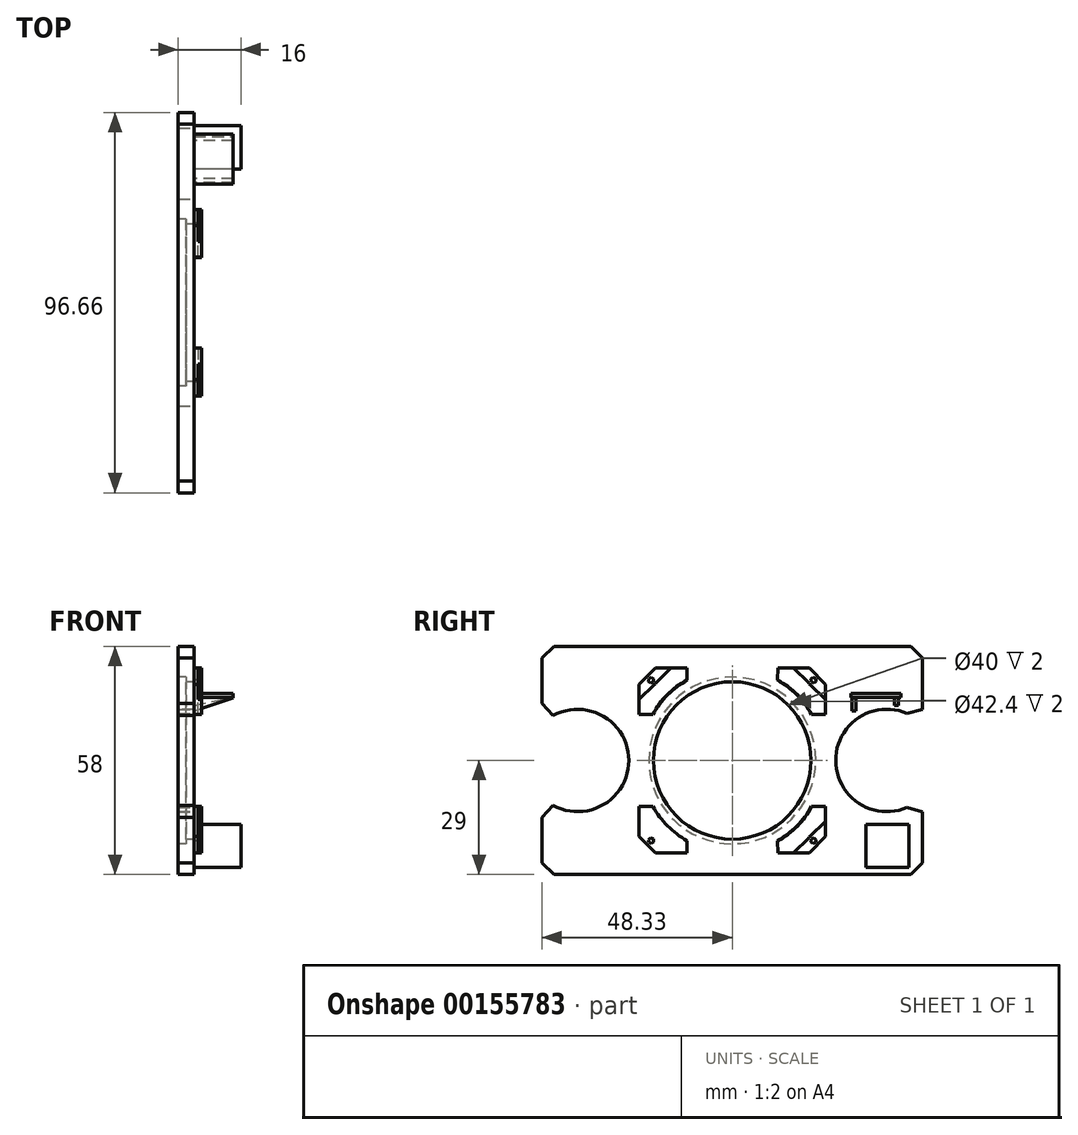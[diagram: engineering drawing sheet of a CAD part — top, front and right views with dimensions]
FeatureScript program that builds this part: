
annotation { "Feature Type Name" : "Feature", "Feature Type Description" : "" }
export const myFeature = defineFeature(function(context is Context, id is Id, definition is map)
    precondition{}
    {
        {
            var Q0;
            Q0=qCreatedBy(makeId("Right.planeOp"),FACE);
            var sketch = newSketch(context, id + "F0", { "sketchPlane" : qUnion([Q0])});
            skLineSegment(sketch, "E0", {"start": v(-0.17, 29) * mm, "end": v(48.33, 29) * mm});
            skCircle(sketch, "E1", {"center": v(0, 0) * mm, "radius": 20 * mm});
            skLineSegment(sketch, "E2", {"start": v(-71.24, 0) * mm, "end": v(71.03, 0) * mm, "construction": true});
            skLineSegment(sketch, "E3", {"start": v(0, -43.54) * mm, "end": v(0, 44.78) * mm, "construction": true});
            skLineSegment(sketch, "E4", {"start": v(48.33, 29) * mm, "end": v(48.33, 0) * mm});
            skLineSegment(sketch, "E5.MirrorCS", {"start": v(0.17, 29) * mm, "end": v(-48.33, 29) * mm});
            skLineSegment(sketch, "E6.MirrorCS", {"start": v(-48.33, 29) * mm, "end": v(-48.33, 0) * mm});
            skLineSegment(sketch, "E7.MirrorCS", {"start": v(-48.33, -29) * mm, "end": v(-48.33, 0) * mm});
            skLineSegment(sketch, "E8.MirrorCS", {"start": v(0.17, -29) * mm, "end": v(-48.33, -29) * mm});
            skLineSegment(sketch, "E9.MirrorCS", {"start": v(-0.17, -29) * mm, "end": v(48.33, -29) * mm});
            skLineSegment(sketch, "E10.MirrorCS", {"start": v(48.33, -29) * mm, "end": v(48.33, 0) * mm});
            skLineSegment(sketch, "E11", {"start": v(-65.88, 28) * mm, "end": v(62.3, 28) * mm, "construction": true});
            skLineSegment(sketch, "E12.MirrorCS", {"start": v(-65.88, -28) * mm, "end": v(62.3, -28) * mm, "construction": true});
            skSolve(sketch);
        }
        {
            var Q0;
            Q0 = qSketchRegion(id + "F0", true);
            extrude(context, id + "F1", {"entities" : qUnion([Q0]), "depth" : 4 * mm});
        }
        {
            var Q0;
            Q0=makeQuery(id+"F1.opExtrude","CAP_FACE",FACE,{"disambiguationData":[OSD([sQuery(id+"F0.wireOp",EDGE,"E0"),sQuery(id+"F0.wireOp",EDGE,"E1"),sQuery(id+"F0.wireOp",EDGE,"E4"),sQuery(id+"F0.wireOp",EDGE,"E5.MirrorCS"),sQuery(id+"F0.wireOp",EDGE,"E6.MirrorCS"),sQuery(id+"F0.wireOp",EDGE,"E7.MirrorCS"),sQuery(id+"F0.wireOp",EDGE,"E8.MirrorCS"),sQuery(id+"F0.wireOp",EDGE,"E9.MirrorCS"),sQuery(id+"F0.wireOp",EDGE,"E10.MirrorCS")])],"isStart":false});
            var sketch = newSketch(context, id + "F2", { "sketchPlane" : qUnion([Q0])});
            skCircle(sketch, "E13", {"center": v(-39.28, 0) * mm, "radius": 13 * mm});
            skLineSegment(sketch, "E14", {"start": v(0, 41.82) * mm, "end": v(0, -40.06) * mm, "construction": true});
            skLineSegment(sketch, "E15", {"start": v(59.88, 0) * mm, "end": v(-62, 0) * mm, "construction": true});
            skCircle(sketch, "E16.MirrorC", {"center": v(39.28, 0) * mm, "radius": 13 * mm});
            skSolve(sketch);
        }
        {
            var Q0;
            Q0 = qSketchRegion(id + "F2", true);
            extrude(context, id + "F3", {"entities" : qUnion([Q0]), "operationType" : NewBodyOperationType.REMOVE, "oppositeDirection" : true, "depth" : 5 * mm});
        }
        {
            var Q0;
            Q0=makeQuery(id+"F3.boolean.opBoolean","INTERSECT",EDGE,{"disambiguationData":[OD(1.0)],"derivedFrom":[makeQuery(id+"F1.opExtrude","SWEPT_FACE",FACE,{"disambiguationData":[OSD([sQuery(id+"F0.wireOp",EDGE,"E4"),sQuery(id+"F0.wireOp",EDGE,"E10.MirrorCS")])]}),makeQuery(id+"F3.opExtrude","SWEPT_FACE",FACE,{"disambiguationData":[OSD([sQuery(id+"F2.wireOp",EDGE,"E16.MirrorC")])]})]});
            var Q1;
            Q1=makeQuery(id+"F3.boolean.opBoolean","INTERSECT",EDGE,{"disambiguationData":[OD(0.0)],"derivedFrom":[makeQuery(id+"F1.opExtrude","SWEPT_FACE",FACE,{"disambiguationData":[OSD([sQuery(id+"F0.wireOp",EDGE,"E4"),sQuery(id+"F0.wireOp",EDGE,"E10.MirrorCS")])]}),makeQuery(id+"F3.opExtrude","SWEPT_FACE",FACE,{"disambiguationData":[OSD([sQuery(id+"F2.wireOp",EDGE,"E16.MirrorC")])]})]});
            chamfer(context, id + "F4", {"entities" : qUnion([Q0, Q1]), "chamferType" : ChamferType.TWO_OFFSETS, "width1" : 6 * mm, "oppositeDirection" : true, "width2" : 5 * mm, "tangentPropagation" : true});
        }
        {
            var Q0;
            Q0=makeQuery(id+"F3.boolean.opBoolean","INTERSECT",EDGE,{"disambiguationData":[OD(1.0)],"derivedFrom":[makeQuery(id+"F1.opExtrude","SWEPT_FACE",FACE,{"disambiguationData":[OSD([sQuery(id+"F0.wireOp",EDGE,"E6.MirrorCS"),sQuery(id+"F0.wireOp",EDGE,"E7.MirrorCS")])]}),makeQuery(id+"F3.opExtrude","SWEPT_FACE",FACE,{"disambiguationData":[OSD([sQuery(id+"F2.wireOp",EDGE,"E13")])]})]});
            var Q1;
            Q1=makeQuery(id+"F3.boolean.opBoolean","INTERSECT",EDGE,{"disambiguationData":[OD(0.0)],"derivedFrom":[makeQuery(id+"F1.opExtrude","SWEPT_FACE",FACE,{"disambiguationData":[OSD([sQuery(id+"F0.wireOp",EDGE,"E6.MirrorCS"),sQuery(id+"F0.wireOp",EDGE,"E7.MirrorCS")])]}),makeQuery(id+"F3.opExtrude","SWEPT_FACE",FACE,{"disambiguationData":[OSD([sQuery(id+"F2.wireOp",EDGE,"E13")])]})]});
            chamfer(context, id + "F5", {"entities" : qUnion([Q0, Q1]), "chamferType" : ChamferType.TWO_OFFSETS, "width1" : 5 * mm, "oppositeDirection" : true, "width2" : 6 * mm, "tangentPropagation" : true});
        }
        {
            var Q0;
            Q0=makeQuery(id+"F1.opExtrude","SWEPT_EDGE",EDGE,{"disambiguationData":[OSD([sQuery(id+"F0.wireOp",EDGE,"E5.MirrorCS"),sQuery(id+"F0.wireOp",EDGE,"E6.MirrorCS")])]});
            var Q1;
            Q1=makeQuery(id+"F1.opExtrude","SWEPT_EDGE",EDGE,{"disambiguationData":[OSD([sQuery(id+"F0.wireOp",EDGE,"E0"),sQuery(id+"F0.wireOp",EDGE,"E4")])]});
            var Q2;
            Q2=makeQuery(id+"F1.opExtrude","SWEPT_EDGE",EDGE,{"disambiguationData":[OSD([sQuery(id+"F0.wireOp",EDGE,"E9.MirrorCS"),sQuery(id+"F0.wireOp",EDGE,"E10.MirrorCS")])]});
            var Q3;
            Q3=makeQuery(id+"F1.opExtrude","SWEPT_EDGE",EDGE,{"disambiguationData":[OSD([sQuery(id+"F0.wireOp",EDGE,"E7.MirrorCS"),sQuery(id+"F0.wireOp",EDGE,"E8.MirrorCS")])]});
            chamfer(context, id + "F6", {"entities" : qUnion([Q0, Q1, Q2, Q3]), "width" : 3 * mm, "tangentPropagation" : true});
        }
        {
            var Q0;
            Q0=makeQuery(id+"F1.opExtrude","CAP_FACE",FACE,{"disambiguationData":[OSD([sQuery(id+"F0.wireOp",EDGE,"E0"),sQuery(id+"F0.wireOp",EDGE,"E1"),sQuery(id+"F0.wireOp",EDGE,"E4"),sQuery(id+"F0.wireOp",EDGE,"E5.MirrorCS"),sQuery(id+"F0.wireOp",EDGE,"E6.MirrorCS"),sQuery(id+"F0.wireOp",EDGE,"E7.MirrorCS"),sQuery(id+"F0.wireOp",EDGE,"E8.MirrorCS"),sQuery(id+"F0.wireOp",EDGE,"E9.MirrorCS"),sQuery(id+"F0.wireOp",EDGE,"E10.MirrorCS")])],"isStart":false});
            var sketch = newSketch(context, id + "F7", { "sketchPlane" : qUnion([Q0])});
            skSolve(sketch);
        }
        {
            var Q0;
            {var subQ7=sQuery(id+"F0.wireOp",EDGE,"E1");Q0=makeQuery(id+"F7.imprint","IMPRINT",FACE,{"disambiguationData":[TD([[makeQuery(id+"F7.imprint","IMPRINT",EDGE,{"derivedFrom":makeQuery(id+"F1.opExtrude","CAP_EDGE",EDGE,{"disambiguationData":[OSD([subQ7])],"isStart":false})}),-1.0]])]});}
            var sketch = newSketch(context, id + "F8", { "sketchPlane" : qUnion([Q0])});
            skLineSegment(sketch, "E17", {"start": v(0, 45.22) * mm, "end": v(0, -42.28) * mm, "construction": true});
            skLineSegment(sketch, "E18", {"start": v(53.44, 0) * mm, "end": v(-45.28, 0) * mm, "construction": true});
            skLineSegment(sketch, "E19", {"start": v(-23.7, 19.27) * mm, "end": v(-23.67, 11.67) * mm});
            skLineSegment(sketch, "E20", {"start": v(-23.67, 11.67) * mm, "end": v(-20.17, 11.7) * mm});
            skLineSegment(sketch, "E21", {"start": v(-19.55, 23.47) * mm, "end": v(-11.55, 23.47) * mm});
            skLineSegment(sketch, "E22", {"start": v(-11.55, 23.47) * mm, "end": v(-11.5, 20.4) * mm});
            skArc(sketch, "E23", {"start": v(-11.5, 20.4) * mm, "mid": v(-16.43, 16.64) * mm, "end": v(-20.17, 11.7) * mm});
            skLineSegment(sketch, "E24", {"start": v(-19.55, 23.47) * mm, "end": v(-23.7, 19.27) * mm});
            skLineSegment(sketch, "E25", {"start": v(0, 0) * mm, "end": v(-36.4, 36.4) * mm, "construction": true});
            skLineSegment(sketch, "E26.MirrorCS", {"start": v(19.55, 23.47) * mm, "end": v(11.55, 23.47) * mm});
            skLineSegment(sketch, "E27.MirrorCS", {"start": v(11.55, 23.47) * mm, "end": v(11.5, 20.4) * mm});
            skLineSegment(sketch, "E28.MirrorCS", {"start": v(19.55, 23.47) * mm, "end": v(23.7, 19.27) * mm});
            skArc(sketch, "E29.MirrorCS", {"start": v(11.5, 20.4) * mm, "mid": v(16.43, 16.64) * mm, "end": v(20.17, 11.7) * mm});
            skLineSegment(sketch, "E30.MirrorCS", {"start": v(23.67, 11.67) * mm, "end": v(20.17, 11.7) * mm});
            skLineSegment(sketch, "E31.MirrorCS", {"start": v(23.7, 19.27) * mm, "end": v(23.67, 11.67) * mm});
            skLineSegment(sketch, "E32.MirrorCS", {"start": v(-23.67, -11.67) * mm, "end": v(-20.17, -11.7) * mm});
            skArc(sketch, "E33.MirrorCS", {"start": v(-11.5, -20.4) * mm, "mid": v(-16.43, -16.64) * mm, "end": v(-20.17, -11.7) * mm});
            skLineSegment(sketch, "E34.MirrorCS", {"start": v(-11.55, -23.47) * mm, "end": v(-11.5, -20.4) * mm});
            skLineSegment(sketch, "E35.MirrorCS", {"start": v(-19.55, -23.47) * mm, "end": v(-11.55, -23.47) * mm});
            skLineSegment(sketch, "E36.MirrorCS", {"start": v(-19.55, -23.47) * mm, "end": v(-23.7, -19.27) * mm});
            skLineSegment(sketch, "E37.MirrorCS", {"start": v(-23.7, -19.27) * mm, "end": v(-23.67, -11.67) * mm});
            skLineSegment(sketch, "E38.MirrorCS", {"start": v(11.55, -23.47) * mm, "end": v(11.5, -20.4) * mm});
            skLineSegment(sketch, "E39.MirrorCS", {"start": v(19.55, -23.47) * mm, "end": v(11.55, -23.47) * mm});
            skLineSegment(sketch, "E40.MirrorCS", {"start": v(19.55, -23.47) * mm, "end": v(23.7, -19.27) * mm});
            skLineSegment(sketch, "E41.MirrorCS", {"start": v(23.7, -19.27) * mm, "end": v(23.67, -11.67) * mm});
            skLineSegment(sketch, "E42.MirrorCS", {"start": v(23.67, -11.67) * mm, "end": v(20.17, -11.7) * mm});
            skArc(sketch, "E43.MirrorCS", {"start": v(11.5, -20.4) * mm, "mid": v(16.43, -16.64) * mm, "end": v(20.17, -11.7) * mm});
            skSolve(sketch);
        }
        {
            var Q0;
            Q0 = qSketchRegion(id + "F8", true);
            extrude(context, id + "F9", {"entities" : qUnion([Q0]), "operationType" : NewBodyOperationType.ADD, "depth" : 1 * mm});
        }
        {
            var Q0;
            Q0=makeQuery(id+"F9.opExtrude","CAP_FACE",FACE,{"disambiguationData":[OSD([sQuery(id+"F8.wireOp",EDGE,"E19"),sQuery(id+"F8.wireOp",EDGE,"E20"),sQuery(id+"F8.wireOp",EDGE,"E21"),sQuery(id+"F8.wireOp",EDGE,"E22"),sQuery(id+"F8.wireOp",EDGE,"E23"),sQuery(id+"F8.wireOp",EDGE,"E24")])],"isStart":false});
            var sketch = newSketch(context, id + "F10", { "sketchPlane" : qUnion([Q0])});
            skLineSegment(sketch, "E44", {"start": v(0, 25.38) * mm, "end": v(0, -25.1) * mm, "construction": true});
            skLineSegment(sketch, "E45", {"start": v(28.15, 0) * mm, "end": v(-31.21, 0) * mm, "construction": true});
            skLineSegment(sketch, "E46", {"start": v(-15.55, 23.47) * mm, "end": v(-23.68, 15.47) * mm});
            skLineSegment(sketch, "E47", {"start": v(-23.68, 15.47) * mm, "end": v(-23.67, 11.67) * mm});
            skLineSegment(sketch, "E48", {"start": v(-23.67, 11.67) * mm, "end": v(-20.17, 11.7) * mm});
            skLineSegment(sketch, "E49", {"start": v(-15.55, 23.47) * mm, "end": v(-11.55, 23.47) * mm});
            skLineSegment(sketch, "E50", {"start": v(-11.55, 23.47) * mm, "end": v(-11.5, 20.4) * mm});
            skArc(sketch, "E51", {"start": v(-11.5, 20.4) * mm, "mid": v(-16.5, 16.71) * mm, "end": v(-20.17, 11.7) * mm});
            skLineSegment(sketch, "E52", {"start": v(-21.62, 21.37) * mm, "end": v(-16.43, 16.64) * mm, "construction": true});
            skCircle(sketch, "E53.cCircle", {"center": v(-20.17, 20.04) * mm, "radius": 0.8 * mm, "construction": true});
            skLineSegment(sketch, "E53.0", {"start": v(-21.04, 19.77) * mm, "end": v(-20.84, 20.66) * mm});
            skLineSegment(sketch, "E53.1", {"start": v(-20.84, 20.66) * mm, "end": v(-19.97, 20.94) * mm});
            skLineSegment(sketch, "E53.2", {"start": v(-19.97, 20.94) * mm, "end": v(-19.3, 20.32) * mm});
            skLineSegment(sketch, "E53.3", {"start": v(-19.3, 20.32) * mm, "end": v(-19.49, 19.43) * mm});
            skLineSegment(sketch, "E53.4", {"start": v(-19.49, 19.43) * mm, "end": v(-20.36, 19.15) * mm});
            skLineSegment(sketch, "E53.5", {"start": v(-20.36, 19.15) * mm, "end": v(-21.04, 19.77) * mm});
            skPoint(sketch, "E53.0.midPoint", {"position": v(-20.94, 20.21) * mm});
            skLineSegment(sketch, "E54.MirrorCS", {"start": v(11.55, 23.47) * mm, "end": v(11.5, 20.4) * mm});
            skLineSegment(sketch, "E55.MirrorCS", {"start": v(15.55, 23.47) * mm, "end": v(11.55, 23.47) * mm});
            skLineSegment(sketch, "E56.MirrorCS", {"start": v(15.55, 23.47) * mm, "end": v(23.68, 15.47) * mm});
            skLineSegment(sketch, "E57.MirrorCS", {"start": v(23.68, 15.47) * mm, "end": v(23.67, 11.67) * mm});
            skLineSegment(sketch, "E58.MirrorCS", {"start": v(23.67, 11.67) * mm, "end": v(20.17, 11.7) * mm});
            skArc(sketch, "E59.MirrorCS", {"start": v(11.5, 20.4) * mm, "mid": v(16.5, 16.71) * mm, "end": v(20.17, 11.7) * mm});
            skCircle(sketch, "E60.MirrorC", {"center": v(20.17, 20.04) * mm, "radius": 0.8 * mm, "construction": true});
            skLineSegment(sketch, "E61.MirrorCS", {"start": v(19.3, 20.32) * mm, "end": v(19.49, 19.43) * mm});
            skLineSegment(sketch, "E62.MirrorCS", {"start": v(19.49, 19.43) * mm, "end": v(20.36, 19.15) * mm});
            skLineSegment(sketch, "E63.MirrorCS", {"start": v(20.36, 19.15) * mm, "end": v(21.04, 19.77) * mm});
            skLineSegment(sketch, "E64.MirrorCS", {"start": v(21.04, 19.77) * mm, "end": v(20.84, 20.66) * mm});
            skLineSegment(sketch, "E65.MirrorCS", {"start": v(20.84, 20.66) * mm, "end": v(19.97, 20.94) * mm});
            skLineSegment(sketch, "E66.MirrorCS", {"start": v(19.97, 20.94) * mm, "end": v(19.3, 20.32) * mm});
            skLineSegment(sketch, "E67.MirrorCS", {"start": v(23.67, -11.67) * mm, "end": v(20.17, -11.7) * mm});
            skLineSegment(sketch, "E68.MirrorCS", {"start": v(23.68, -15.47) * mm, "end": v(23.67, -11.67) * mm});
            skLineSegment(sketch, "E69.MirrorCS", {"start": v(15.55, -23.47) * mm, "end": v(23.68, -15.47) * mm});
            skArc(sketch, "E70.MirrorCS", {"start": v(11.5, -20.4) * mm, "mid": v(16.5, -16.71) * mm, "end": v(20.17, -11.7) * mm});
            skLineSegment(sketch, "E71.MirrorCS", {"start": v(11.55, -23.47) * mm, "end": v(11.5, -20.4) * mm});
            skLineSegment(sketch, "E72.MirrorCS", {"start": v(15.55, -23.47) * mm, "end": v(11.55, -23.47) * mm});
            skLineSegment(sketch, "E73.MirrorCS", {"start": v(19.3, -20.32) * mm, "end": v(19.49, -19.43) * mm});
            skLineSegment(sketch, "E74.MirrorCS", {"start": v(19.97, -20.94) * mm, "end": v(19.3, -20.32) * mm});
            skLineSegment(sketch, "E75.MirrorCS", {"start": v(20.84, -20.66) * mm, "end": v(19.97, -20.94) * mm});
            skLineSegment(sketch, "E76.MirrorCS", {"start": v(21.04, -19.77) * mm, "end": v(20.84, -20.66) * mm});
            skLineSegment(sketch, "E77.MirrorCS", {"start": v(20.36, -19.15) * mm, "end": v(21.04, -19.77) * mm});
            skLineSegment(sketch, "E78.MirrorCS", {"start": v(19.49, -19.43) * mm, "end": v(20.36, -19.15) * mm});
            skArc(sketch, "E79.MirrorCS", {"start": v(-11.5, -20.4) * mm, "mid": v(-16.5, -16.71) * mm, "end": v(-20.17, -11.7) * mm});
            skLineSegment(sketch, "E80.MirrorCS", {"start": v(-11.55, -23.47) * mm, "end": v(-11.5, -20.4) * mm});
            skLineSegment(sketch, "E81.MirrorCS", {"start": v(-15.55, -23.47) * mm, "end": v(-11.55, -23.47) * mm});
            skLineSegment(sketch, "E82.MirrorCS", {"start": v(-15.55, -23.47) * mm, "end": v(-23.68, -15.47) * mm});
            skLineSegment(sketch, "E83.MirrorCS", {"start": v(-23.68, -15.47) * mm, "end": v(-23.67, -11.67) * mm});
            skLineSegment(sketch, "E84.MirrorCS", {"start": v(-23.67, -11.67) * mm, "end": v(-20.17, -11.7) * mm});
            skLineSegment(sketch, "E85.MirrorCS", {"start": v(-21.04, -19.77) * mm, "end": v(-20.84, -20.66) * mm});
            skLineSegment(sketch, "E86.MirrorCS", {"start": v(-20.84, -20.66) * mm, "end": v(-19.97, -20.94) * mm});
            skLineSegment(sketch, "E87.MirrorCS", {"start": v(-19.97, -20.94) * mm, "end": v(-19.3, -20.32) * mm});
            skLineSegment(sketch, "E88.MirrorCS", {"start": v(-19.3, -20.32) * mm, "end": v(-19.49, -19.43) * mm});
            skLineSegment(sketch, "E89.MirrorCS", {"start": v(-19.49, -19.43) * mm, "end": v(-20.36, -19.15) * mm});
            skLineSegment(sketch, "E90.MirrorCS", {"start": v(-20.36, -19.15) * mm, "end": v(-21.04, -19.77) * mm});
            skSolve(sketch);
        }
        {
            var Q0;
            Q0=makeQuery(id+"F10.imprint","IMPRINT",FACE,{"disambiguationData":[TD([[makeQuery(id+"F10.imprint","IMPRINT",EDGE,{"derivedFrom":sQuery(id+"F10.wireOp",EDGE,"E79.MirrorCS")}),1.0]])]});
            var Q1;
            Q1=makeQuery(id+"F10.imprint","IMPRINT",FACE,{"disambiguationData":[TD([[makeQuery(id+"F10.imprint","IMPRINT",EDGE,{"derivedFrom":sQuery(id+"F10.wireOp",EDGE,"E67.MirrorCS")}),1.0]])]});
            var Q2;
            Q2=makeQuery(id+"F10.imprint","IMPRINT",FACE,{"disambiguationData":[TD([[makeQuery(id+"F10.imprint","IMPRINT",EDGE,{"derivedFrom":sQuery(id+"F10.wireOp",EDGE,"E54.MirrorCS")}),1.0]])]});
            var Q3;
            Q3=makeQuery(id+"F10.imprint","IMPRINT",FACE,{"disambiguationData":[TD([[makeQuery(id+"F10.imprint","IMPRINT",EDGE,{"derivedFrom":sQuery(id+"F10.wireOp",EDGE,"E46")}),1.0]])]});
            extrude(context, id + "F11", {"entities" : qUnion([Q0, Q1, Q2, Q3]), "operationType" : NewBodyOperationType.ADD, "depth" : 1 * mm});
        }
        {
            var Q0;
            {var subQ0=sQuery(id+"F8.wireOp",EDGE,"E24");var subQ1=sQuery(id+"F8.wireOp",EDGE,"E21");var subQ2=sQuery(id+"F8.wireOp",EDGE,"E19");Q0=makeQuery(id+"F11.boolean.opBoolean","SPLIT",FACE,{"disambiguationData":[TD([makeQuery(id+"F9.opExtrude","SWEPT_FACE",FACE,{"disambiguationData":[OSD([subQ2])]})])],"derivedFrom":makeQuery(id+"F9.opExtrude","CAP_FACE",FACE,{"disambiguationData":[OSD([subQ2,sQuery(id+"F8.wireOp",EDGE,"E20"),subQ1,sQuery(id+"F8.wireOp",EDGE,"E22"),sQuery(id+"F8.wireOp",EDGE,"E23"),subQ0])],"isStart":false})});}
            var sketch = newSketch(context, id + "F12", { "sketchPlane" : qUnion([Q0])});
            skLineSegment(sketch, "E91", {"start": v(-21.62, 21.37) * mm, "end": v(-19.66, 19.43) * mm, "construction": true});
            skCircle(sketch, "E92.cCircle", {"center": v(-20.64, 20.4) * mm, "radius": 0.71 * mm, "construction": true});
            skLineSegment(sketch, "E92.0", {"start": v(-20.08, 19.96) * mm, "end": v(-20.74, 19.7) * mm});
            skLineSegment(sketch, "E92.1", {"start": v(-20.74, 19.7) * mm, "end": v(-21.3, 20.13) * mm});
            skLineSegment(sketch, "E92.2", {"start": v(-21.3, 20.13) * mm, "end": v(-21.2, 20.84) * mm});
            skLineSegment(sketch, "E92.3", {"start": v(-21.2, 20.84) * mm, "end": v(-20.54, 21.1) * mm});
            skLineSegment(sketch, "E92.4", {"start": v(-20.54, 21.1) * mm, "end": v(-19.98, 20.67) * mm});
            skLineSegment(sketch, "E92.5", {"start": v(-19.98, 20.67) * mm, "end": v(-20.08, 19.96) * mm});
            skLineSegment(sketch, "E93", {"start": v(0, 29.9) * mm, "end": v(0, 13.87) * mm, "construction": true});
            skLineSegment(sketch, "E94.MirrorCS", {"start": v(21.3, 20.13) * mm, "end": v(21.2, 20.84) * mm});
            skLineSegment(sketch, "E95.MirrorCS", {"start": v(20.74, 19.7) * mm, "end": v(21.3, 20.13) * mm});
            skLineSegment(sketch, "E96.MirrorCS", {"start": v(20.08, 19.96) * mm, "end": v(20.74, 19.7) * mm});
            skLineSegment(sketch, "E97.MirrorCS", {"start": v(19.98, 20.67) * mm, "end": v(20.08, 19.96) * mm});
            skLineSegment(sketch, "E98.MirrorCS", {"start": v(20.54, 21.1) * mm, "end": v(19.98, 20.67) * mm});
            skLineSegment(sketch, "E99.MirrorCS", {"start": v(21.2, 20.84) * mm, "end": v(20.54, 21.1) * mm});
            skLineSegment(sketch, "E100", {"start": v(-29.02, 0) * mm, "end": v(29.07, 0) * mm, "construction": true});
            skLineSegment(sketch, "E101.MirrorCS", {"start": v(21.3, -20.13) * mm, "end": v(21.2, -20.84) * mm});
            skLineSegment(sketch, "E102.MirrorCS", {"start": v(20.54, -21.1) * mm, "end": v(19.98, -20.67) * mm});
            skLineSegment(sketch, "E103.MirrorCS", {"start": v(19.98, -20.67) * mm, "end": v(20.08, -19.96) * mm});
            skLineSegment(sketch, "E104.MirrorCS", {"start": v(20.08, -19.96) * mm, "end": v(20.74, -19.7) * mm});
            skLineSegment(sketch, "E105.MirrorCS", {"start": v(20.74, -19.7) * mm, "end": v(21.3, -20.13) * mm});
            skLineSegment(sketch, "E106.MirrorCS", {"start": v(21.2, -20.84) * mm, "end": v(20.54, -21.1) * mm});
            skLineSegment(sketch, "E107", {"start": v(0, -11.03) * mm, "end": v(0, -24.21) * mm, "construction": true});
            skLineSegment(sketch, "E108.MirrorCS", {"start": v(-19.98, -20.67) * mm, "end": v(-20.08, -19.96) * mm});
            skLineSegment(sketch, "E109.MirrorCS", {"start": v(-20.54, -21.1) * mm, "end": v(-19.98, -20.67) * mm});
            skLineSegment(sketch, "E110.MirrorCS", {"start": v(-21.2, -20.84) * mm, "end": v(-20.54, -21.1) * mm});
            skLineSegment(sketch, "E111.MirrorCS", {"start": v(-21.3, -20.13) * mm, "end": v(-21.2, -20.84) * mm});
            skLineSegment(sketch, "E112.MirrorCS", {"start": v(-20.74, -19.7) * mm, "end": v(-21.3, -20.13) * mm});
            skLineSegment(sketch, "E113.MirrorCS", {"start": v(-20.08, -19.96) * mm, "end": v(-20.74, -19.7) * mm});
            skSolve(sketch);
        }
        {
            var Q0;
            Q0 = qSketchRegion(id + "F12", true);
            extrude(context, id + "F13", {"entities" : qUnion([Q0]), "operationType" : NewBodyOperationType.ADD, "depth" : .5 * mm});
        }
        {
            var Q0;
            {var subQ7=sQuery(id+"F0.wireOp",EDGE,"E1");Q0=makeQuery(id+"F7.imprint","IMPRINT",FACE,{"disambiguationData":[TD([[makeQuery(id+"F7.imprint","IMPRINT",EDGE,{"derivedFrom":makeQuery(id+"F1.opExtrude","CAP_EDGE",EDGE,{"disambiguationData":[OSD([subQ7])],"isStart":false})}),-1.0]])]});}
            var sketch = newSketch(context, id + "F14", { "sketchPlane" : qUnion([Q0])});
            skLineSegment(sketch, "E114", {"start": v(44.94, -16.22) * mm, "end": v(33.94, -16.22) * mm});
            skLineSegment(sketch, "E115", {"start": v(33.94, -16.22) * mm, "end": v(33.94, -27.22) * mm});
            skLineSegment(sketch, "E116", {"start": v(33.94, -27.22) * mm, "end": v(44.94, -27.22) * mm});
            skLineSegment(sketch, "E117", {"start": v(44.94, -27.22) * mm, "end": v(44.94, -16.22) * mm});
            skSolve(sketch);
        }
        {
            var Q0;
            Q0 = qSketchRegion(id + "F14", true);
            extrude(context, id + "F15", {"entities" : qUnion([Q0]), "operationType" : NewBodyOperationType.ADD, "depth" : 12 * mm});
        }
        {
            var Q0;
            {var subQ7=sQuery(id+"F0.wireOp",EDGE,"E1");Q0=makeQuery(id+"F7.imprint","IMPRINT",FACE,{"disambiguationData":[TD([[makeQuery(id+"F7.imprint","IMPRINT",EDGE,{"derivedFrom":makeQuery(id+"F1.opExtrude","CAP_EDGE",EDGE,{"disambiguationData":[OSD([subQ7])],"isStart":false})}),-1.0]])]});}
            var sketch = newSketch(context, id + "F16", { "sketchPlane" : qUnion([Q0])});
            skLineSegment(sketch, "E118", {"start": v(30.12, 17.07) * mm, "end": v(30.12, 16.07) * mm});
            skLineSegment(sketch, "E119", {"start": v(30.12, 16.07) * mm, "end": v(42.82, 16.07) * mm});
            skLineSegment(sketch, "E120", {"start": v(42.82, 16.07) * mm, "end": v(42.82, 17.07) * mm});
            skLineSegment(sketch, "E121", {"start": v(42.82, 17.07) * mm, "end": v(30.12, 17.07) * mm});
            skSolve(sketch);
        }
        {
            var Q0;
            Q0 = qSketchRegion(id + "F16", true);
            extrude(context, id + "F17", {"entities" : qUnion([Q0]), "operationType" : NewBodyOperationType.ADD, "depth" : 10 * mm});
        }
        {
            var Q0;
            {var subQ7=sQuery(id+"F0.wireOp",EDGE,"E1");Q0=makeQuery(id+"F7.imprint","IMPRINT",FACE,{"disambiguationData":[TD([[makeQuery(id+"F7.imprint","IMPRINT",EDGE,{"derivedFrom":makeQuery(id+"F1.opExtrude","CAP_EDGE",EDGE,{"disambiguationData":[OSD([subQ7])],"isStart":false})}),-1.0]])]});}
            var sketch = newSketch(context, id + "F18", { "sketchPlane" : qUnion([Q0])});
            skLineSegment(sketch, "E122", {"start": v(30.44, 16.04) * mm, "end": v(30.44, 10.86) * mm});
            skLineSegment(sketch, "E123", {"start": v(30.44, 10.86) * mm, "end": v(31.44, 10.86) * mm});
            skLineSegment(sketch, "E124", {"start": v(31.44, 10.86) * mm, "end": v(31.44, 16.04) * mm});
            skLineSegment(sketch, "E125", {"start": v(31.44, 16.04) * mm, "end": v(30.44, 16.04) * mm});
            skLineSegment(sketch, "E126", {"start": v(42.18, 16.04) * mm, "end": v(42.18, 13.03) * mm});
            skLineSegment(sketch, "E127", {"start": v(42.18, 13.03) * mm, "end": v(41.18, 13.03) * mm});
            skLineSegment(sketch, "E128", {"start": v(41.18, 13.03) * mm, "end": v(41.18, 16.04) * mm});
            skLineSegment(sketch, "E129", {"start": v(41.18, 16.04) * mm, "end": v(42.18, 16.04) * mm});
            skSolve(sketch);
        }
        {
            var Q0;
            Q0 = qSketchRegion(id + "F18", true);
            extrude(context, id + "F19", {"entities" : qUnion([Q0]), "operationType" : NewBodyOperationType.ADD, "depth" : 10 * mm});
        }
        {
            var Q0;
            Q0=makeQuery(id+"F19.opExtrude","CAP_EDGE",EDGE,{"disambiguationData":[OSD([sQuery(id+"F18.wireOp",EDGE,"E127")])],"isStart":false});
            chamfer(context, id + "F20", {"entities" : qUnion([Q0]), "chamferType" : ChamferType.TWO_OFFSETS, "width1" : 3 * mm, "oppositeDirection" : true, "width2" : 15 * mm, "tangentPropagation" : true});
        }
        {
            var Q0;
            Q0=makeQuery(id+"F19.opExtrude","CAP_EDGE",EDGE,{"disambiguationData":[OSD([sQuery(id+"F18.wireOp",EDGE,"E123")])],"isStart":false});
            chamfer(context, id + "F21", {"entities" : qUnion([Q0]), "chamferType" : ChamferType.TWO_OFFSETS, "width1" : 15 * mm, "oppositeDirection" : true, "width2" : 5 * mm, "tangentPropagation" : true});
        }
        {
            var Q0;
            Q0=makeQuery(id+"F1.opExtrude","CAP_FACE",FACE,{"disambiguationData":[OSD([sQuery(id+"F0.wireOp",EDGE,"E0"),sQuery(id+"F0.wireOp",EDGE,"E1"),sQuery(id+"F0.wireOp",EDGE,"E4"),sQuery(id+"F0.wireOp",EDGE,"E5.MirrorCS"),sQuery(id+"F0.wireOp",EDGE,"E6.MirrorCS"),sQuery(id+"F0.wireOp",EDGE,"E7.MirrorCS"),sQuery(id+"F0.wireOp",EDGE,"E8.MirrorCS"),sQuery(id+"F0.wireOp",EDGE,"E9.MirrorCS"),sQuery(id+"F0.wireOp",EDGE,"E10.MirrorCS")])],"isStart":true});
            var sketch = newSketch(context, id + "F22", { "sketchPlane" : qUnion([Q0])});
            skCircle(sketch, "E130", {"center": v(0, 0) * mm, "radius": 21.2 * mm});
            skCircle(sketch, "E131", {"center": v(0, 0) * mm, "radius": 20 * mm});
            skSolve(sketch);
        }
        {
            var Q0;
            Q0 = qSketchRegion(id + "F22", true);
            extrude(context, id + "F23", {"entities" : qUnion([Q0]), "operationType" : NewBodyOperationType.REMOVE, "oppositeDirection" : true, "depth" : 2 * mm});
        }
    });
